# Revit family: ALN440 Pendant Mount
name_source: partatom
category: Lighting Fixtures
units: mm (PartAtom-declared; Revit-internal decimal feet)

## family parameters
Cut with Voids When Loaded = No
Host = Face
Light Source = No
OmniClass Number = 23.80.70.14
OmniClass Title = Luminaries for External Lighting
Part Type = Normal
Room Calculation Point = No
Round Connector Dimension = Use Diameter
Shared = No

## types (13) — shared parameters
Apparent Load = 50 VA
Default Elevation = 48.000"
Description = The Towne Commons family of fixtures are available in a wide range of sizes and configurations
Lamp = ED-17 & T-6 ceramic MH
Light Bulb Material = Glass
Load Classification = Lighting
Manufacturer = Architectural Area Lighting
Model = ALN440D
URL = https://www.currentlighting.com
Wattage Comments = 50-150W

## per-type parameters (varying)
| type | Finish |
| Antique Green | Aluminum-Antique Green |
| Artic White | Aluminum-Artic White |
| Black | Aluminum-Black |
| Matte Black | Aluminum-Matte Black |
| Dark Green | Aluminum-Dark Green |
| Dark Bronze | Aluminum-Dark Bronze |
| Weathered Bronze | Aluminum-Metalic Bronze |
| Metalic Bronze | Aluminum-Metalic Bronze |
| Verde Blue | Aluminum-Verde Blue |
| Corten | Aluminum-Corten |
| Matte Aluminum | Matte Aluminum |
| Medium Grey | Aluminum-Medium Grey |
| Light Grey | Aluminum-Light Grey |

## geometry (parser evidence)
native form markers: Blend x29, Sweep x7
no freeform markers — native parametric forms only
